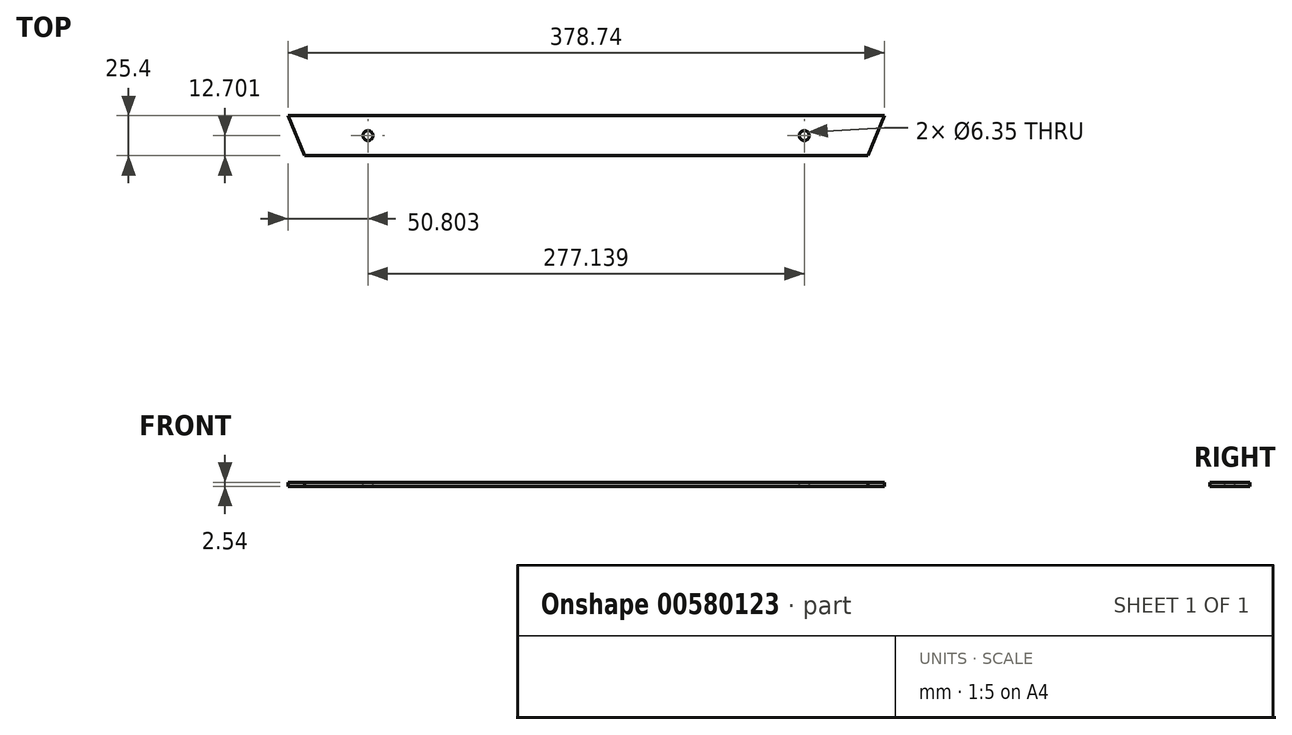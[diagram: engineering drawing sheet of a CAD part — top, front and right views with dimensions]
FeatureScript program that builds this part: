
annotation { "Feature Type Name" : "Feature", "Feature Type Description" : "" }
export const myFeature = defineFeature(function(context is Context, id is Id, definition is map)
    precondition{}
    {
        {
            var Q0;
            Q0=qCreatedBy(makeId("Top.planeOp"),FACE);
            var sketch = newSketch(context, id + "F0", { "sketchPlane" : qUnion([Q0])});
            skLineSegment(sketch, "E0.bottom", {"start": v(-147.37, -21.76) * mm, "end": v(231.37, -21.76) * mm});
            skLineSegment(sketch, "E0.top", {"start": v(-147.37, -47.16) * mm, "end": v(231.37, -47.16) * mm});
            skLineSegment(sketch, "E0.left", {"start": v(-147.37, -21.76) * mm, "end": v(-147.37, -47.16) * mm});
            skLineSegment(sketch, "E0.right", {"start": v(231.37, -21.76) * mm, "end": v(231.37, -47.16) * mm});
            skSolve(sketch);
        }
        {
            var Q0;
            Q0=qSketchRegion(id+"F0",true);
            extrude(context, id + "F1", {"entities" : qUnion([Q0]), "depth" : 2.54 * mm, "offsetDistance" : 25.4 * mm});
        }
        {
            var Q0;
            Q0=makeQuery(id+"F1.opExtrude","CAP_FACE",FACE,{"disambiguationData":[OSD([sQuery(id+"F0.wireOp",EDGE,"E0.bottom"),sQuery(id+"F0.wireOp",EDGE,"E0.top"),sQuery(id+"F0.wireOp",EDGE,"E0.left"),sQuery(id+"F0.wireOp",EDGE,"E0.right")])],"isStart":false});
            var sketch = newSketch(context, id + "F2", { "sketchPlane" : qUnion([Q0])});
            skLineSegment(sketch, "E1", {"start": v(-147.37, -21.76) * mm, "end": v(-136.85, -47.16) * mm});
            skLineSegment(sketch, "E2", {"start": v(231.37, -21.76) * mm, "end": v(220.85, -47.16) * mm});
            skLineSegment(sketch, "E3", {"start": v(220.85, -47.16) * mm, "end": v(231.37, -47.16) * mm});
            skLineSegment(sketch, "E4", {"start": v(-136.85, -47.16) * mm, "end": v(-147.37, -47.16) * mm});
            skSolve(sketch);
        }
        {
            var Q0;
            Q0=makeQuery(id+"F2.imprint","IMPRINT",FACE,{"disambiguationData":[TD([[makeQuery(id+"F2.imprint","IMPRINT",EDGE,{"derivedFrom":sQuery(id+"F2.wireOp",EDGE,"E1")}),-1.0]])]});
            var Q1;
            Q1=makeQuery(id+"F2.imprint","IMPRINT",FACE,{"disambiguationData":[TD([[makeQuery(id+"F2.imprint","IMPRINT",EDGE,{"derivedFrom":sQuery(id+"F2.wireOp",EDGE,"E2")}),1.0]])]});
            extrude(context, id + "F3", {"entities" : qUnion([Q0, Q1]), "operationType" : NewBodyOperationType.REMOVE, "endBound" : BoundingType.THROUGH_ALL, "oppositeDirection" : true, "depth" : 25.4 * mm, "offsetDistance" : 25.4 * mm});
        }
        {
            var Q0;
            Q0=makeQuery(id+"F1.opExtrude","CAP_FACE",FACE,{"disambiguationData":[OSD([sQuery(id+"F0.wireOp",EDGE,"E0.bottom"),sQuery(id+"F0.wireOp",EDGE,"E0.top"),sQuery(id+"F0.wireOp",EDGE,"E0.left"),sQuery(id+"F0.wireOp",EDGE,"E0.right")])],"isStart":false});
            var sketch = newSketch(context, id + "F4", { "sketchPlane" : qUnion([Q0])});
            skCircle(sketch, "E5", {"center": v(-96.57, -34.46) * mm, "radius": 3.18 * mm});
            skCircle(sketch, "E6", {"center": v(180.57, -34.46) * mm, "radius": 3.17 * mm});
            skLineSegment(sketch, "E7", {"start": v(-99.31, -32.86) * mm, "end": v(-96.57, -34.46) * mm});
            skLineSegment(sketch, "E8", {"start": v(180.57, -34.46) * mm, "end": v(177.4, -34.46) * mm});
            skSolve(sketch);
        }
        {
            var Q0;
            Q0=qSketchRegion(id+"F4",true);
            extrude(context, id + "F5", {"entities" : qUnion([Q0]), "operationType" : NewBodyOperationType.REMOVE, "endBound" : BoundingType.THROUGH_ALL, "oppositeDirection" : true, "depth" : 25.4 * mm, "offsetDistance" : 25.4 * mm});
        }
    });
